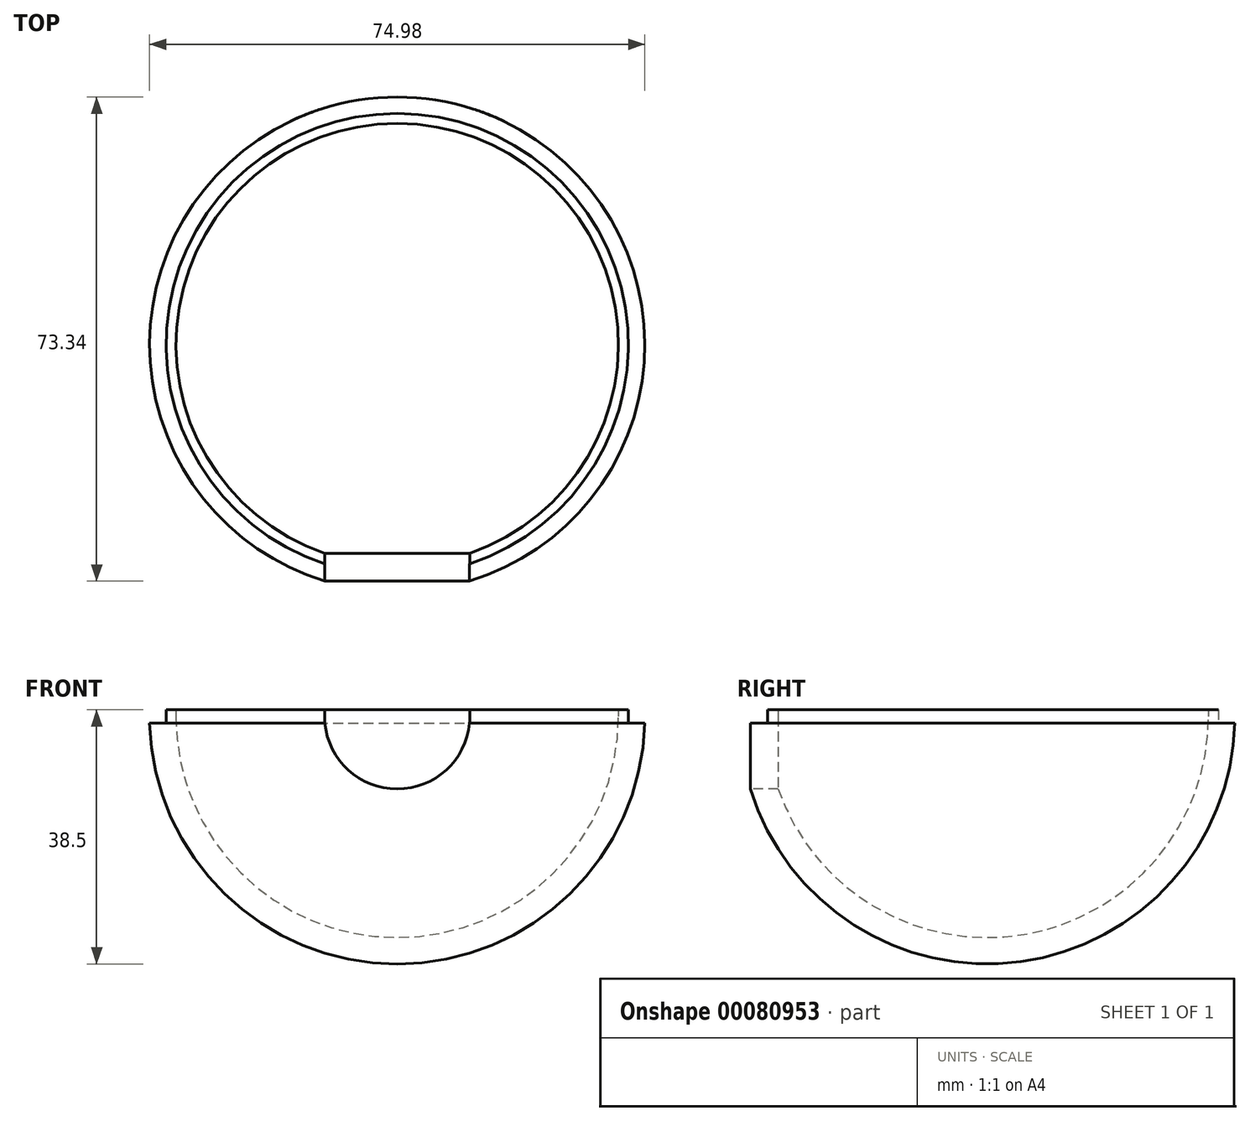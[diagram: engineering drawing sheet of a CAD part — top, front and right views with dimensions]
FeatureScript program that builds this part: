
annotation { "Feature Type Name" : "Feature", "Feature Type Description" : "" }
export const myFeature = defineFeature(function(context is Context, id is Id, definition is map)
    precondition{}
    {
        {
            var Q0;
            Q0=qCreatedBy(makeId("Top.planeOp"),FACE);
            var sketch = newSketch(context, id + "F0", { "sketchPlane" : qUnion([Q0])});
            skCircle(sketch, "E0", {"center": v(0, 0) * mm, "radius": 37.5 * mm});
            skCircle(sketch, "E1.0", {"center": v(0, 0) * mm, "radius": 33.5 * mm});
            skCircle(sketch, "E2", {"center": v(0, 0) * mm, "radius": 35 * mm});
            skLineSegment(sketch, "E3", {"start": v(0, 37.5) * mm, "end": v(0, -37.5) * mm, "construction": true});
            skLineSegment(sketch, "E4", {"start": v(0, -37.5) * mm, "end": v(0, -33.5) * mm});
            skLineSegment(sketch, "E5", {"start": v(0, 37.5) * mm, "end": v(0, 33.5) * mm});
            skLineSegment(sketch, "E6", {"start": v(-11, -35.85) * mm, "end": v(-11, -31.64) * mm});
            skLineSegment(sketch, "E7.MirrorCS", {"start": v(11, -35.85) * mm, "end": v(11, -31.64) * mm});
            skSolve(sketch);
        }
        {
            var Q0;
            {var subQ0=sQuery(id+"F0.wireOp",EDGE,"E5");var subQ1=sQuery(id+"F0.wireOp",EDGE,"E0");var subQ2=makeQuery(id+"F0.imprint","INTERSECT",VERTEX,{"derivedFrom":[subQ1,subQ0]});Q0=makeQuery(id+"F0.imprint","IMPRINT",FACE,{"disambiguationData":[TD([[makeQuery(id+"F0.imprint","IMPRINT",EDGE,{"disambiguationData":[TD([[subQ2,-1.0]])],"derivedFrom":subQ1}),1.0]])]});}
            var Q1;
            {var subQ0=sQuery(id+"F0.wireOp",EDGE,"E5");var subQ1=sQuery(id+"F0.wireOp",EDGE,"E1.0");var subQ2=makeQuery(id+"F0.imprint","INTERSECT",VERTEX,{"derivedFrom":[subQ1,subQ0]});Q1=makeQuery(id+"F0.imprint","IMPRINT",FACE,{"disambiguationData":[TD([[makeQuery(id+"F0.imprint","IMPRINT",EDGE,{"disambiguationData":[TD([[subQ2,-1.0]])],"derivedFrom":subQ1}),-1.0]])]});}
            var Q2;
            Q2=sQuery(id+"F0.wireOp",EDGE,"E3");
            revolve(context, id + "F1", {"entities" : qUnion([Q0, Q1]), "axis" : qUnion([Q2]), "revolveType" : RevolveType.ONE_DIRECTION, "oppositeDirection" : true, "angle" : 180 * degree});
        }
        {
            var Q0;
            {var subQ0=sQuery(id+"F0.wireOp",EDGE,"E5");var subQ1=sQuery(id+"F0.wireOp",EDGE,"E1.0");var subQ2=makeQuery(id+"F0.imprint","INTERSECT",VERTEX,{"derivedFrom":[subQ1,subQ0]});Q0=makeQuery(id+"F0.imprint","IMPRINT",FACE,{"disambiguationData":[TD([[makeQuery(id+"F0.imprint","IMPRINT",EDGE,{"disambiguationData":[TD([[subQ2,-1.0]])],"derivedFrom":subQ1}),-1.0]])]});}
            var Q1;
            {var subQ0=sQuery(id+"F0.wireOp",EDGE,"E5");var subQ1=sQuery(id+"F0.wireOp",EDGE,"E1.0");var subQ2=makeQuery(id+"F0.imprint","INTERSECT",VERTEX,{"derivedFrom":[subQ1,subQ0]});Q1=makeQuery(id+"F0.imprint","IMPRINT",FACE,{"disambiguationData":[TD([[makeQuery(id+"F0.imprint","IMPRINT",EDGE,{"disambiguationData":[TD([[subQ2,1.0]])],"derivedFrom":subQ1}),-1.0]])]});}
            extrude(context, id + "F2", {"entities" : qUnion([Q0, Q1]), "operationType" : NewBodyOperationType.ADD, "oppositeDirection" : true, "depth" : 1 * mm});
        }
        {
            var Q0;
            {var subQ0=sQuery(id+"F0.wireOp",EDGE,"E5");var subQ1=sQuery(id+"F0.wireOp",EDGE,"E0");var subQ2=makeQuery(id+"F0.imprint","INTERSECT",VERTEX,{"derivedFrom":[subQ1,subQ0]});Q0=makeQuery(id+"F0.imprint","IMPRINT",FACE,{"disambiguationData":[TD([[makeQuery(id+"F0.imprint","IMPRINT",EDGE,{"disambiguationData":[TD([[subQ2,-1.0]])],"derivedFrom":subQ1}),1.0]])]});}
            var Q1;
            {var subQ0=sQuery(id+"F0.wireOp",EDGE,"E5");var subQ1=sQuery(id+"F0.wireOp",EDGE,"E0");var subQ2=makeQuery(id+"F0.imprint","INTERSECT",VERTEX,{"derivedFrom":[subQ1,subQ0]});Q1=makeQuery(id+"F0.imprint","IMPRINT",FACE,{"disambiguationData":[TD([[makeQuery(id+"F0.imprint","IMPRINT",EDGE,{"disambiguationData":[TD([[subQ2,1.0]])],"derivedFrom":subQ1}),1.0]])]});}
            var Q2;
            {var subQ0=sQuery(id+"F0.wireOp",EDGE,"E4");var subQ1=sQuery(id+"F0.wireOp",EDGE,"E0");var subQ2=makeQuery(id+"F0.imprint","INTERSECT",VERTEX,{"derivedFrom":[subQ1,subQ0]});Q2=makeQuery(id+"F0.imprint","IMPRINT",FACE,{"disambiguationData":[TD([[makeQuery(id+"F0.imprint","IMPRINT",EDGE,{"disambiguationData":[TD([[subQ2,1.0]])],"derivedFrom":subQ1}),1.0]])]});}
            var Q3;
            {var subQ0=sQuery(id+"F0.wireOp",EDGE,"E4");var subQ1=sQuery(id+"F0.wireOp",EDGE,"E0");var subQ2=makeQuery(id+"F0.imprint","INTERSECT",VERTEX,{"derivedFrom":[subQ1,subQ0]});Q3=makeQuery(id+"F0.imprint","IMPRINT",FACE,{"disambiguationData":[TD([[makeQuery(id+"F0.imprint","IMPRINT",EDGE,{"disambiguationData":[TD([[subQ2,-1.0]])],"derivedFrom":subQ1}),1.0]])]});}
            extrude(context, id + "F3", {"entities" : qUnion([Q0, Q1, Q2, Q3]), "operationType" : NewBodyOperationType.REMOVE, "depth" : 1 * mm});
        }
        {
            var Q0;
            Q0=makeQuery(id+"F1.opRevolve","SWEPT_BODY",BODY,{"disambiguationData":[OSD([sQuery(id+"F0.wireOp",EDGE,"E0"),sQuery(id+"F0.wireOp",EDGE,"E1.0"),sQuery(id+"F0.wireOp",EDGE,"E5"),sQuery(id+"F0.wireOp",EDGE,"E6")])]});
            var Q1;
            Q1=sQuery(id+"F0.wireOp",EDGE,"E3");
            transform(context, id + "F4", {"entities" : qUnion([Q0]), "transformType" : TransformType.ROTATION, "transformAxis" : qUnion([Q1]), "angle" : 180 * degree, "makeCopy" : false});
        }
    });
